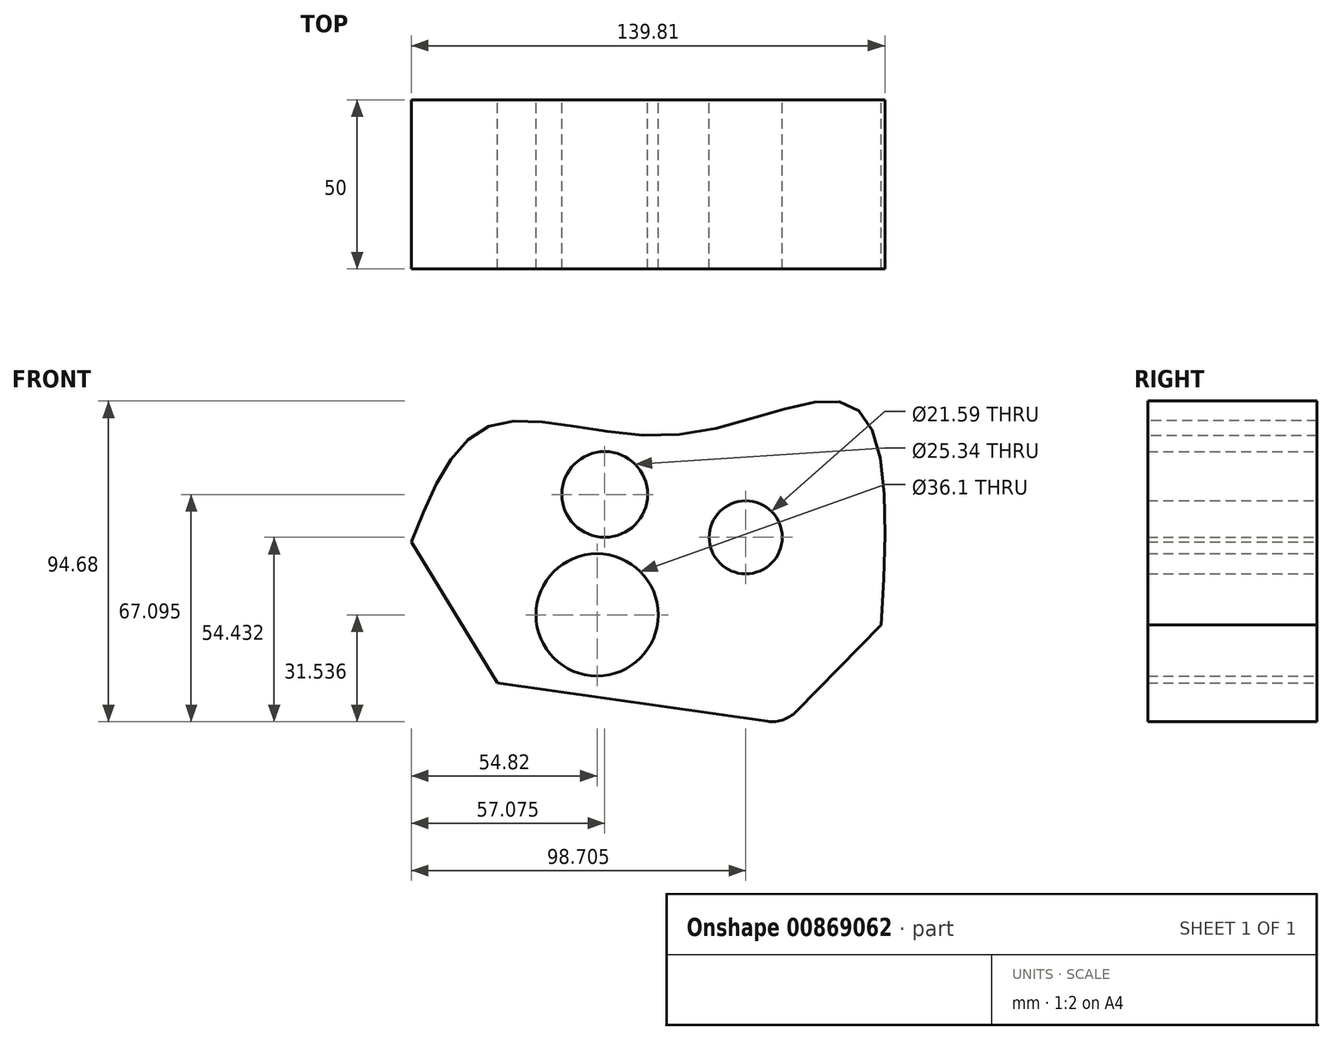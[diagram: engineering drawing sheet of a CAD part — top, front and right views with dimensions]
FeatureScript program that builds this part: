
annotation { "Feature Type Name" : "Feature", "Feature Type Description" : "" }
export const myFeature = defineFeature(function(context is Context, id is Id, definition is map)
    precondition{}
    {
        {
            var Q0;
            Q0=qCreatedBy(makeId("Front.planeOp"),FACE);
            var sketch = newSketch(context, id + "F0", { "sketchPlane" : qUnion([Q0])});
            skFitSpline(sketch, "E0", {"points": [v(-68.09, 11.06) * mm, v(-44.65, 45.4) * mm, v(10.14, 42.67) * mm, v(62.2, 51.12) * mm, v(70.64, -13.47) * mm], "startDerivative": vector(80.97, 204.37) * mm, "endDerivative": vector(-16.94, -315.37) * mm});
            skLineSegment(sketch, "E1", {"start": v(-68.09, 11.06) * mm, "end": v(-42.74, -30.64) * mm});
            skLineSegment(sketch, "E2", {"start": v(-42.74, -30.64) * mm, "end": v(42.02, -42.64) * mm});
            skLineSegment(sketch, "E3", {"start": v(42.02, -42.64) * mm, "end": v(70.64, -13.47) * mm});
            skCircle(sketch, "E4", {"center": v(-11.01, 25.06) * mm, "radius": 12.67 * mm});
            skCircle(sketch, "E5", {"center": v(30.62, 12.4) * mm, "radius": 10.8 * mm});
            skCircle(sketch, "E6", {"center": v(-13.27, -10.5) * mm, "radius": 18.05 * mm});
            skSolve(sketch);
        }
        {
            var Q0;
            Q0=makeQuery(id+"F0.imprint","IMPRINT",FACE,{"disambiguationData":[TD([[makeQuery(id+"F0.imprint","IMPRINT",EDGE,{"derivedFrom":sQuery(id+"F0.wireOp",EDGE,"E0")}),-1.0]])]});
            extrude(context, id + "F1", {"entities" : qUnion([Q0]), "depth" : 50 * mm, "offsetDistance" : 25 * mm});
        }
        {
            var Q0;
            Q0=makeQuery(id+"F1.opExtrude","SWEPT_EDGE",EDGE,{"disambiguationData":[OSD([sQuery(id+"F0.wireOp",EDGE,"E2"),sQuery(id+"F0.wireOp",EDGE,"E3")])]});
            fillet(context, id + "F2", {"entities" : qUnion([Q0]), "radius" : 10 * mm, "tangentPropagation" : true, "allowEdgeOverflow" : false});
        }
    });
